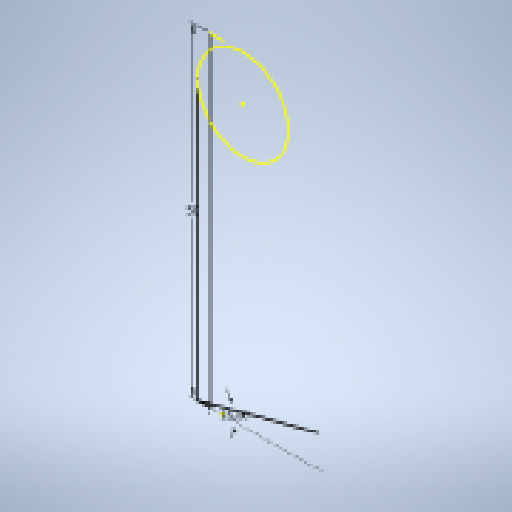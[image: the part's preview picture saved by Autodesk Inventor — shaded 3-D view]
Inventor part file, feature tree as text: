
AUTODESK INVENTOR PART (.ipt)
format: ipt  version: 2023 (Build 270158000, 158)  size: 144,896 bytes
history: native  units: in
note: dims shown in document units (in); Inventor stores cm internally (conversion verified against a paired STEP export)
features: other x6, reference x3, extrude x1, sketch x1
ambient origin geometry x8: Origin, YZ Plane, XZ Plane, XY Plane, X Axis, Y Axis, Z Axis, Center Point
bodies: Body1 (feature_tree)
feature tree (11):
  other  "Bryła1"
  extrude  "Wyciągnięcie proste1"  Depth=1.9685in
  sketch  "Szkic1"
  reference  "Odniesienie1"
  reference  "Odniesienie2"
  reference  "Odniesienie3"
  other  "<userpath>\Documents\Inventor\MikroNalesnik\byk.iam"
  other  "byk.iam"
  other  "kolko:2"
  other  "spod:1"
  other  "pcb:1"
